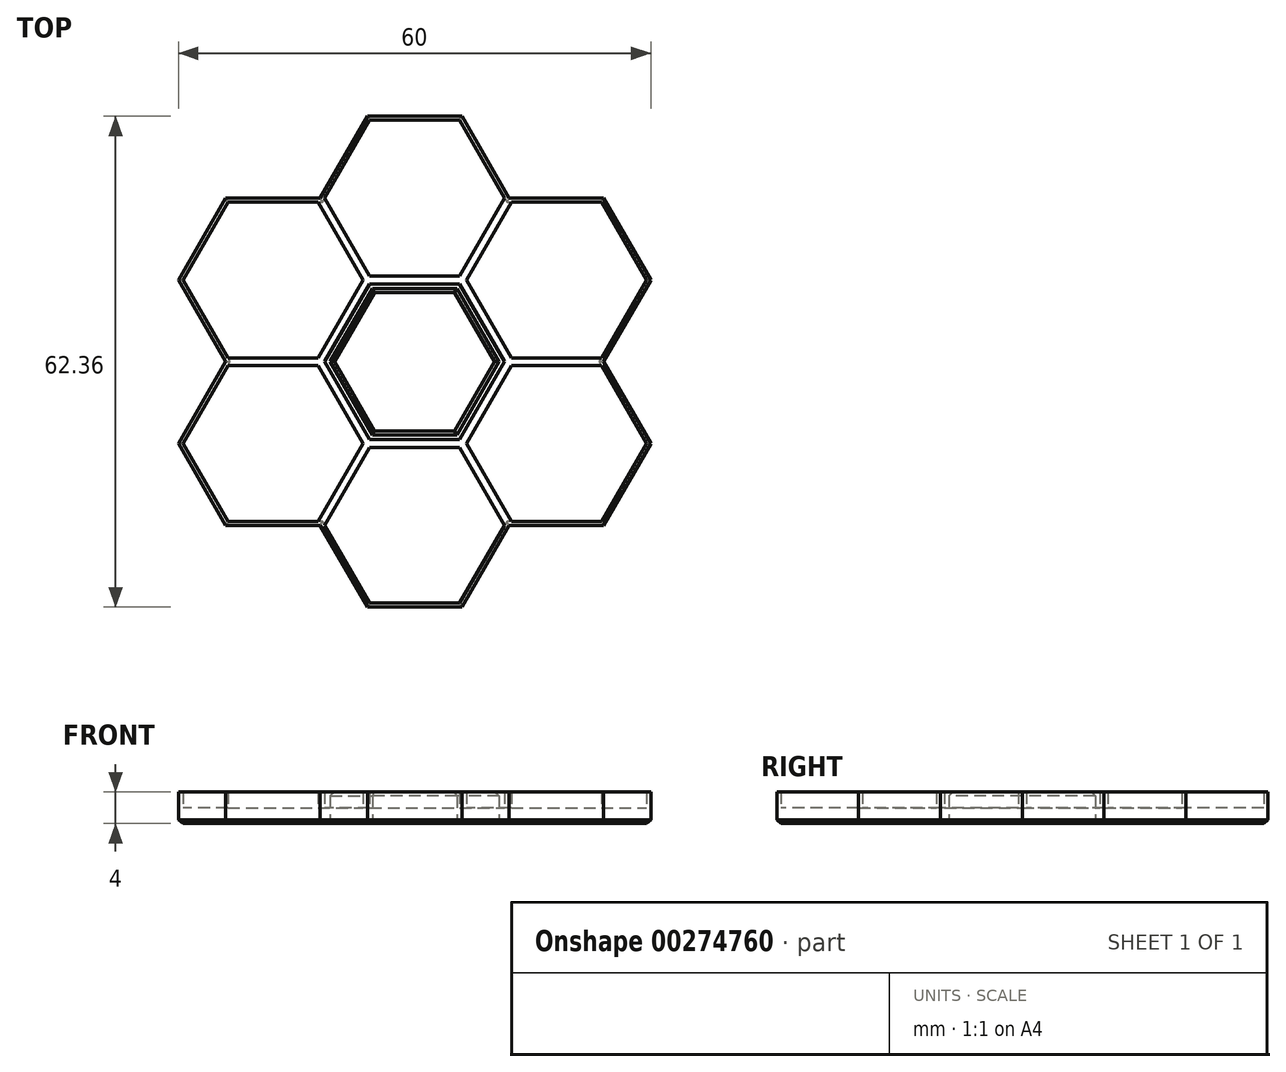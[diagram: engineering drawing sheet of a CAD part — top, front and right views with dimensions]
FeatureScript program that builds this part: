
annotation { "Feature Type Name" : "Feature", "Feature Type Description" : "" }
export const myFeature = defineFeature(function(context is Context, id is Id, definition is map)
    precondition{}
    {
        {
            var Q0;
            Q0=qCreatedBy(makeId("Top.planeOp"),FACE);
            var sketch = newSketch(context, id + "F0", { "sketchPlane" : qUnion([Q0])});
            skCircle(sketch, "E0.cCircle", {"center": v(0, 0) * mm, "radius": 10.4 * mm, "construction": true});
            skLineSegment(sketch, "E0.0", {"start": v(6, -10.4) * mm, "end": v(-6, -10.4) * mm});
            skLineSegment(sketch, "E0.1", {"start": v(-6, -10.4) * mm, "end": v(-12, 0) * mm});
            skLineSegment(sketch, "E0.2", {"start": v(-12, 0) * mm, "end": v(-6, 10.4) * mm});
            skLineSegment(sketch, "E0.3", {"start": v(-6, 10.4) * mm, "end": v(6, 10.4) * mm});
            skLineSegment(sketch, "E0.4", {"start": v(6, 10.4) * mm, "end": v(12, 0) * mm});
            skLineSegment(sketch, "E0.5", {"start": v(12, 0) * mm, "end": v(6, -10.4) * mm});
            skPoint(sketch, "E0.0.midPoint", {"position": v(0, -10.4) * mm});
            skLineSegment(sketch, "E1.0", {"start": v(-5.71, -9.9) * mm, "end": v(-11.42, 0) * mm});
            skLineSegment(sketch, "E1.1", {"start": v(-5.71, 9.9) * mm, "end": v(5.71, 9.9) * mm});
            skLineSegment(sketch, "E1.2", {"start": v(5.71, 9.9) * mm, "end": v(11.42, 0) * mm});
            skLineSegment(sketch, "E1.3", {"start": v(-11.42, 0) * mm, "end": v(-5.71, 9.9) * mm});
            skLineSegment(sketch, "E1.4", {"start": v(11.42, 0) * mm, "end": v(5.71, -9.9) * mm});
            skLineSegment(sketch, "E1.5", {"start": v(5.71, -9.9) * mm, "end": v(-5.71, -9.9) * mm});
            skSolve(sketch);
        }
        {
            var Q0;
            Q0=makeQuery(id+"F0.imprint","IMPRINT",FACE,{"disambiguationData":[TD([[makeQuery(id+"F0.imprint","IMPRINT",EDGE,{"derivedFrom":sQuery(id+"F0.wireOp",EDGE,"E0.0")}),-1.0]])]});
            extrude(context, id + "F1", {"entities" : qUnion([Q0]), "depth" : 4 * mm});
        }
        {
            var Q0;
            Q0=makeQuery(id+"F0.imprint","IMPRINT",FACE,{"disambiguationData":[TD([[makeQuery(id+"F0.imprint","IMPRINT",EDGE,{"derivedFrom":sQuery(id+"F0.wireOp",EDGE,"E1.0")}),-1.0]])]});
            extrude(context, id + "F2", {"entities" : qUnion([Q0]), "operationType" : NewBodyOperationType.ADD, "depth" : 2 * mm});
        }
        {
            var Q0;
            Q0=makeQuery(id+"F1.opExtrude","SWEPT_BODY",BODY,{"disambiguationData":[OSD([sQuery(id+"F0.wireOp",EDGE,"E0.0"),sQuery(id+"F0.wireOp",EDGE,"E0.1"),sQuery(id+"F0.wireOp",EDGE,"E0.2"),sQuery(id+"F0.wireOp",EDGE,"E0.3"),sQuery(id+"F0.wireOp",EDGE,"E0.4"),sQuery(id+"F0.wireOp",EDGE,"E0.5"),sQuery(id+"F0.wireOp",EDGE,"E1.0"),sQuery(id+"F0.wireOp",EDGE,"E1.1"),sQuery(id+"F0.wireOp",EDGE,"E1.2"),sQuery(id+"F0.wireOp",EDGE,"E1.3"),sQuery(id+"F0.wireOp",EDGE,"E1.4"),sQuery(id+"F0.wireOp",EDGE,"E1.5")])]});
            var Q1;
            Q1=makeQuery(id+"F1.opExtrude","SWEPT_EDGE",EDGE,{"disambiguationData":[OSD([sQuery(id+"F0.wireOp",EDGE,"E0.0"),sQuery(id+"F0.wireOp",EDGE,"E0.5")])]});
            circularPattern(context, id + "F3", {"entities" : qUnion([Q0]), "axis" : qUnion([Q1]), "angle" : 360 * degree, "instanceCount" : 3, "equalSpace" : true});
        }
        {
            var Q0;
            Q0=makeQuery(id+"F1.opExtrude","SWEPT_BODY",BODY,{"disambiguationData":[OSD([sQuery(id+"F0.wireOp",EDGE,"E0.0"),sQuery(id+"F0.wireOp",EDGE,"E0.1"),sQuery(id+"F0.wireOp",EDGE,"E0.2"),sQuery(id+"F0.wireOp",EDGE,"E0.3"),sQuery(id+"F0.wireOp",EDGE,"E0.4"),sQuery(id+"F0.wireOp",EDGE,"E0.5"),sQuery(id+"F0.wireOp",EDGE,"E1.0"),sQuery(id+"F0.wireOp",EDGE,"E1.1"),sQuery(id+"F0.wireOp",EDGE,"E1.2"),sQuery(id+"F0.wireOp",EDGE,"E1.3"),sQuery(id+"F0.wireOp",EDGE,"E1.4"),sQuery(id+"F0.wireOp",EDGE,"E1.5")])]});
            var Q1;
            Q1=makeQuery(id+"F1.opExtrude","SWEPT_EDGE",EDGE,{"disambiguationData":[OSD([sQuery(id+"F0.wireOp",EDGE,"E0.3"),sQuery(id+"F0.wireOp",EDGE,"E0.4")])]});
            circularPattern(context, id + "F4", {"entities" : qUnion([Q0]), "axis" : qUnion([Q1]), "angle" : 360 * degree, "instanceCount" : 3, "equalSpace" : true});
        }
        {
            var Q0;
            Q0=makeQuery(id+"F1.opExtrude","SWEPT_BODY",BODY,{"disambiguationData":[OSD([sQuery(id+"F0.wireOp",EDGE,"E0.0"),sQuery(id+"F0.wireOp",EDGE,"E0.1"),sQuery(id+"F0.wireOp",EDGE,"E0.2"),sQuery(id+"F0.wireOp",EDGE,"E0.3"),sQuery(id+"F0.wireOp",EDGE,"E0.4"),sQuery(id+"F0.wireOp",EDGE,"E0.5"),sQuery(id+"F0.wireOp",EDGE,"E1.0"),sQuery(id+"F0.wireOp",EDGE,"E1.1"),sQuery(id+"F0.wireOp",EDGE,"E1.2"),sQuery(id+"F0.wireOp",EDGE,"E1.3"),sQuery(id+"F0.wireOp",EDGE,"E1.4"),sQuery(id+"F0.wireOp",EDGE,"E1.5")])]});
            var Q1;
            Q1=makeQuery(id+"F1.opExtrude","SWEPT_EDGE",EDGE,{"disambiguationData":[OSD([sQuery(id+"F0.wireOp",EDGE,"E0.1"),sQuery(id+"F0.wireOp",EDGE,"E0.2")])]});
            circularPattern(context, id + "F5", {"entities" : qUnion([Q0]), "axis" : qUnion([Q1]), "angle" : 360 * degree, "instanceCount" : 3, "equalSpace" : true});
        }
        {
            var Q0;
            Q0=makeQuery(id+"F1.opExtrude","SWEPT_BODY",BODY,{"disambiguationData":[OSD([sQuery(id+"F0.wireOp",EDGE,"E0.0"),sQuery(id+"F0.wireOp",EDGE,"E0.1"),sQuery(id+"F0.wireOp",EDGE,"E0.2"),sQuery(id+"F0.wireOp",EDGE,"E0.3"),sQuery(id+"F0.wireOp",EDGE,"E0.4"),sQuery(id+"F0.wireOp",EDGE,"E0.5"),sQuery(id+"F0.wireOp",EDGE,"E1.0"),sQuery(id+"F0.wireOp",EDGE,"E1.1"),sQuery(id+"F0.wireOp",EDGE,"E1.2"),sQuery(id+"F0.wireOp",EDGE,"E1.3"),sQuery(id+"F0.wireOp",EDGE,"E1.4"),sQuery(id+"F0.wireOp",EDGE,"E1.5")])]});
            var Q1;
            Q1=makeQuery(id+"F3.opPattern","COPY",BODY,{"derivedFrom":makeQuery(id+"F1.opExtrude","SWEPT_BODY",BODY,{"disambiguationData":[OSD([sQuery(id+"F0.wireOp",EDGE,"E0.0"),sQuery(id+"F0.wireOp",EDGE,"E0.1"),sQuery(id+"F0.wireOp",EDGE,"E0.2"),sQuery(id+"F0.wireOp",EDGE,"E0.3"),sQuery(id+"F0.wireOp",EDGE,"E0.4"),sQuery(id+"F0.wireOp",EDGE,"E0.5"),sQuery(id+"F0.wireOp",EDGE,"E1.0"),sQuery(id+"F0.wireOp",EDGE,"E1.1"),sQuery(id+"F0.wireOp",EDGE,"E1.2"),sQuery(id+"F0.wireOp",EDGE,"E1.3"),sQuery(id+"F0.wireOp",EDGE,"E1.4"),sQuery(id+"F0.wireOp",EDGE,"E1.5")])]}),"instanceName":"1"});
            var Q2;
            Q2=makeQuery(id+"F4.opPattern","COPY",BODY,{"derivedFrom":makeQuery(id+"F1.opExtrude","SWEPT_BODY",BODY,{"disambiguationData":[OSD([sQuery(id+"F0.wireOp",EDGE,"E0.0"),sQuery(id+"F0.wireOp",EDGE,"E0.1"),sQuery(id+"F0.wireOp",EDGE,"E0.2"),sQuery(id+"F0.wireOp",EDGE,"E0.3"),sQuery(id+"F0.wireOp",EDGE,"E0.4"),sQuery(id+"F0.wireOp",EDGE,"E0.5"),sQuery(id+"F0.wireOp",EDGE,"E1.0"),sQuery(id+"F0.wireOp",EDGE,"E1.1"),sQuery(id+"F0.wireOp",EDGE,"E1.2"),sQuery(id+"F0.wireOp",EDGE,"E1.3"),sQuery(id+"F0.wireOp",EDGE,"E1.4"),sQuery(id+"F0.wireOp",EDGE,"E1.5")])]}),"instanceName":"1"});
            var Q3;
            Q3=makeQuery(id+"F3.opPattern","COPY",BODY,{"derivedFrom":makeQuery(id+"F1.opExtrude","SWEPT_BODY",BODY,{"disambiguationData":[OSD([sQuery(id+"F0.wireOp",EDGE,"E0.0"),sQuery(id+"F0.wireOp",EDGE,"E0.1"),sQuery(id+"F0.wireOp",EDGE,"E0.2"),sQuery(id+"F0.wireOp",EDGE,"E0.3"),sQuery(id+"F0.wireOp",EDGE,"E0.4"),sQuery(id+"F0.wireOp",EDGE,"E0.5"),sQuery(id+"F0.wireOp",EDGE,"E1.0"),sQuery(id+"F0.wireOp",EDGE,"E1.1"),sQuery(id+"F0.wireOp",EDGE,"E1.2"),sQuery(id+"F0.wireOp",EDGE,"E1.3"),sQuery(id+"F0.wireOp",EDGE,"E1.4"),sQuery(id+"F0.wireOp",EDGE,"E1.5")])]}),"instanceName":"2"});
            var Q4;
            Q4=makeQuery(id+"F5.opPattern","COPY",BODY,{"derivedFrom":makeQuery(id+"F1.opExtrude","SWEPT_BODY",BODY,{"disambiguationData":[OSD([sQuery(id+"F0.wireOp",EDGE,"E0.0"),sQuery(id+"F0.wireOp",EDGE,"E0.1"),sQuery(id+"F0.wireOp",EDGE,"E0.2"),sQuery(id+"F0.wireOp",EDGE,"E0.3"),sQuery(id+"F0.wireOp",EDGE,"E0.4"),sQuery(id+"F0.wireOp",EDGE,"E0.5"),sQuery(id+"F0.wireOp",EDGE,"E1.0"),sQuery(id+"F0.wireOp",EDGE,"E1.1"),sQuery(id+"F0.wireOp",EDGE,"E1.2"),sQuery(id+"F0.wireOp",EDGE,"E1.3"),sQuery(id+"F0.wireOp",EDGE,"E1.4"),sQuery(id+"F0.wireOp",EDGE,"E1.5")])]}),"instanceName":"1"});
            var Q5;
            Q5=makeQuery(id+"F4.opPattern","COPY",BODY,{"derivedFrom":makeQuery(id+"F1.opExtrude","SWEPT_BODY",BODY,{"disambiguationData":[OSD([sQuery(id+"F0.wireOp",EDGE,"E0.0"),sQuery(id+"F0.wireOp",EDGE,"E0.1"),sQuery(id+"F0.wireOp",EDGE,"E0.2"),sQuery(id+"F0.wireOp",EDGE,"E0.3"),sQuery(id+"F0.wireOp",EDGE,"E0.4"),sQuery(id+"F0.wireOp",EDGE,"E0.5"),sQuery(id+"F0.wireOp",EDGE,"E1.0"),sQuery(id+"F0.wireOp",EDGE,"E1.1"),sQuery(id+"F0.wireOp",EDGE,"E1.2"),sQuery(id+"F0.wireOp",EDGE,"E1.3"),sQuery(id+"F0.wireOp",EDGE,"E1.4"),sQuery(id+"F0.wireOp",EDGE,"E1.5")])]}),"instanceName":"2"});
            var Q6;
            Q6=makeQuery(id+"F5.opPattern","COPY",BODY,{"derivedFrom":makeQuery(id+"F1.opExtrude","SWEPT_BODY",BODY,{"disambiguationData":[OSD([sQuery(id+"F0.wireOp",EDGE,"E0.0"),sQuery(id+"F0.wireOp",EDGE,"E0.1"),sQuery(id+"F0.wireOp",EDGE,"E0.2"),sQuery(id+"F0.wireOp",EDGE,"E0.3"),sQuery(id+"F0.wireOp",EDGE,"E0.4"),sQuery(id+"F0.wireOp",EDGE,"E0.5"),sQuery(id+"F0.wireOp",EDGE,"E1.0"),sQuery(id+"F0.wireOp",EDGE,"E1.1"),sQuery(id+"F0.wireOp",EDGE,"E1.2"),sQuery(id+"F0.wireOp",EDGE,"E1.3"),sQuery(id+"F0.wireOp",EDGE,"E1.4"),sQuery(id+"F0.wireOp",EDGE,"E1.5")])]}),"instanceName":"2"});
            booleanBodies(context, id + "F6", {"operationType" : BooleanOperationType.UNION, "tools" : qUnion([Q0, Q1, Q2, Q3, Q4, Q5, Q6])});
        }
        {
            var Q0;
            {var subQ0=sQuery(id+"F0.wireOp",EDGE,"E1.5");var subQ1=sQuery(id+"F0.wireOp",EDGE,"E1.4");var subQ2=sQuery(id+"F0.wireOp",EDGE,"E1.3");var subQ3=sQuery(id+"F0.wireOp",EDGE,"E1.2");var subQ4=sQuery(id+"F0.wireOp",EDGE,"E1.1");var subQ5=sQuery(id+"F0.wireOp",EDGE,"E1.0");var subQ6=makeQuery(id+"F2.boolean.opBoolean","MERGE",FACE,{"derivedFrom":[makeQuery(id+"F1.opExtrude","CAP_FACE",FACE,{"disambiguationData":[OSD([sQuery(id+"F0.wireOp",EDGE,"E0.0"),sQuery(id+"F0.wireOp",EDGE,"E0.1"),sQuery(id+"F0.wireOp",EDGE,"E0.2"),sQuery(id+"F0.wireOp",EDGE,"E0.3"),sQuery(id+"F0.wireOp",EDGE,"E0.4"),sQuery(id+"F0.wireOp",EDGE,"E0.5"),subQ5,subQ4,subQ3,subQ2,subQ1,subQ0])],"isStart":true}),makeQuery(id+"F2.opExtrude","CAP_FACE",FACE,{"disambiguationData":[OSD([subQ5,subQ4,subQ3,subQ2,subQ1,subQ0])],"isStart":true})]});Q0=makeQuery(id+"F6.opBoolean","MERGE",FACE,{"derivedFrom":[subQ6,makeQuery(id+"F3.opPattern","COPY",FACE,{"derivedFrom":subQ6,"instanceName":"1"}),makeQuery(id+"F3.opPattern","COPY",FACE,{"derivedFrom":subQ6,"instanceName":"2"}),makeQuery(id+"F4.opPattern","COPY",FACE,{"derivedFrom":subQ6,"instanceName":"1"}),makeQuery(id+"F4.opPattern","COPY",FACE,{"derivedFrom":subQ6,"instanceName":"2"}),makeQuery(id+"F5.opPattern","COPY",FACE,{"derivedFrom":subQ6,"instanceName":"1"}),makeQuery(id+"F5.opPattern","COPY",FACE,{"derivedFrom":subQ6,"instanceName":"2"})]});}
            chamfer(context, id + "F7", {"entities" : qUnion([Q0]), "width" : .5 * mm, "tangentPropagation" : true});
        }
        {
            var Q0;
            Q0=qCreatedBy(makeId("Top.planeOp"),FACE);
            var sketch = newSketch(context, id + "F8", { "sketchPlane" : qUnion([Q0])});
            skPoint(sketch, "E2.0", {"position": v(0, 0) * mm});
            skLineSegment(sketch, "E2.1.0", {"start": v(5.71, -9.9) * mm, "end": v(11.42, 0) * mm, "construction": true});
            skLineSegment(sketch, "E2.1.1", {"start": v(11.42, 0) * mm, "end": v(5.71, 9.9) * mm, "construction": true});
            skLineSegment(sketch, "E2.1.2", {"start": v(5.71, 9.9) * mm, "end": v(-5.71, 9.9) * mm, "construction": true});
            skLineSegment(sketch, "E2.1.3", {"start": v(-5.71, 9.9) * mm, "end": v(-11.42, 0) * mm, "construction": true});
            skLineSegment(sketch, "E2.1.4", {"start": v(-11.42, 0) * mm, "end": v(-5.71, -9.9) * mm, "construction": true});
            skLineSegment(sketch, "E2.1.5", {"start": v(-5.71, -9.9) * mm, "end": v(5.71, -9.9) * mm, "construction": true});
            skLineSegment(sketch, "E3.0", {"start": v(-5.36, -9.3) * mm, "end": v(5.36, -9.3) * mm});
            skLineSegment(sketch, "E3.1", {"start": v(10.73, 0) * mm, "end": v(5.36, 9.3) * mm});
            skLineSegment(sketch, "E3.2", {"start": v(5.36, 9.3) * mm, "end": v(-5.36, 9.3) * mm});
            skLineSegment(sketch, "E3.3", {"start": v(5.36, -9.3) * mm, "end": v(10.73, 0) * mm});
            skLineSegment(sketch, "E3.4", {"start": v(-5.36, 9.3) * mm, "end": v(-10.73, 0) * mm});
            skLineSegment(sketch, "E3.5", {"start": v(-10.73, 0) * mm, "end": v(-5.36, -9.3) * mm});
            skSolve(sketch);
        }
        {
            var Q0;
            Q0=makeQuery(id+"F8.imprint","IMPRINT",FACE,{"disambiguationData":[TD([[makeQuery(id+"F8.imprint","IMPRINT",EDGE,{"derivedFrom":sQuery(id+"F8.wireOp",EDGE,"E3.0")}),1.0]])]});
            extrude(context, id + "F9", {"entities" : qUnion([Q0]), "depth" : 4 * mm});
        }
        {
            var Q0;
            Q0=makeQuery(id+"F9.opExtrude","CAP_FACE",FACE,{"disambiguationData":[OSD([sQuery(id+"F8.wireOp",EDGE,"E3.0"),sQuery(id+"F8.wireOp",EDGE,"E3.1"),sQuery(id+"F8.wireOp",EDGE,"E3.2"),sQuery(id+"F8.wireOp",EDGE,"E3.3"),sQuery(id+"F8.wireOp",EDGE,"E3.4"),sQuery(id+"F8.wireOp",EDGE,"E3.5")])],"isStart":false});
            var Q1;
            Q1=makeQuery(id+"F9.opExtrude","CAP_FACE",FACE,{"disambiguationData":[OSD([sQuery(id+"F8.wireOp",EDGE,"E3.0"),sQuery(id+"F8.wireOp",EDGE,"E3.1"),sQuery(id+"F8.wireOp",EDGE,"E3.2"),sQuery(id+"F8.wireOp",EDGE,"E3.3"),sQuery(id+"F8.wireOp",EDGE,"E3.4"),sQuery(id+"F8.wireOp",EDGE,"E3.5")])],"isStart":true});
            chamfer(context, id + "F10", {"entities" : qUnion([Q0, Q1]), "width" : .5 * mm, "tangentPropagation" : true});
        }
    });
